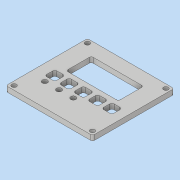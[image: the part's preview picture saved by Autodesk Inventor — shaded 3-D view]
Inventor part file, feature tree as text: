
AUTODESK INVENTOR PART (.ipt)
format: ipt  version: 2018 (Build 220112000, 112)  size: 209,408 bytes
history: native  units: mm
features: sketch x4, reference x3, other x3, extrude x2, hole x2, fillet x2, projected_geometry x1
ambient origin geometry x8: Origin, YZ Plane, XZ Plane, XY Plane, X Axis, Y Axis, Z Axis, Center Point
bodies: Volumenkörper1 (feature_tree)
feature tree (17):
  extrude  "Extrusion1"  Depth=80.0mm
  extrude  "Extrusion3"  Depth=5.0mm
  hole  "Bohrung2"  [1 undecoded]
  hole  "Bohrung3"  [1 undecoded]
  fillet  "Rundung2"  Radius=10.0mm
  fillet  "Rundung1"  Radius=10.0mm
  sketch  "Skizze1"  dims[d0=85.0mm d1=80.0mm]
  sketch  "Skizze3"  dims[d2=5.0mm d3=0.0mm d9=70.0mm]
  sketch  "Skizze5"  dims[d10=62.0mm d12=51.3mm]
  projected_geometry  "Projizierte Kontur1"
  sketch  "Skizze6"  dims[d13=24.7mm d14=4.15mm d15=10.0mm d16=10.0mm d21=8.0mm d22=23.5mm d23=14.0mm d24=14.0mm d25=14.0mm d26=14.0mm d27=5.0mm d28=0.0mm d29=2.1mm d39=4.0mm d40=4.5mm d41=6.0mm d42=4.0mm d43=2.0mm d44=90.0deg d45=8.0mm d46=20.594885mm d47=2.0mm d48=5.0mm d49=6.0mm d50=4.0mm d51=2.0mm d52=90.0deg d53=8.0mm d54=20.594885mm]
  reference  "Referenz7"
  reference  "Referenz8"
  reference  "Referenz9"
  other  "<userpath>\Documents\Waage\CAD\Main.iam"
  other  "Main.iam"
  other  "WaagePCB:1"
note: 2 required parameter values undecoded (feature->parameter linkage not recoverable at this tier; creation-order binding heuristic only, values carry confidence <= 0.55)
